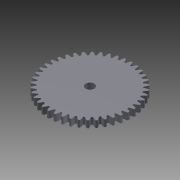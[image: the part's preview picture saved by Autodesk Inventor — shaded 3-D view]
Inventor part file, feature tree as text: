
AUTODESK INVENTOR PART (.ipt)
format: ipt  version: 2014 (Build 180170000, 170)  size: 294,912 bytes
history: native  units: mm (DEFAULTED — no unit token found)
features: plane x3, other x3, sketch x3, extrude x2
ambient origin geometry x8: Origin, YZ Plane, XZ Plane, XY Plane, X Axis, Y Axis, Z Axis, Center Point
bodies: Solid1 (feature_tree)
feature tree (11):
  extrude  "Extrusion1"  Depth=4.0mm TaperAngle=0.0deg
  plane  "Work Plane2"
  plane  "Work Plane8"
  plane  "Work Plane9"
  other  "平歯車"
  extrude  "押し出し2"  Depth=10.0mm TaperAngle=0.0deg
  sketch  "Sketch1"  dims[d0=50.25mm d1=4.0mm d2=0.0mm]
  sketch  "Sketch2"  dims[d3=47.727273mm d4=10.0mm d5=0.0mm d16=37.5mm d17=0.0mm d34=0.747998mm d39=0.0mm d41=0.0mm d43=37.5mm d46=37.5mm d47=0.0mm d48=0.0mm d49=5.2mm d50=10.0mm d51=0.0mm]
  other  "Srf1"
  sketch  "スケッチ3"
  other  "ピッチ円直径"
